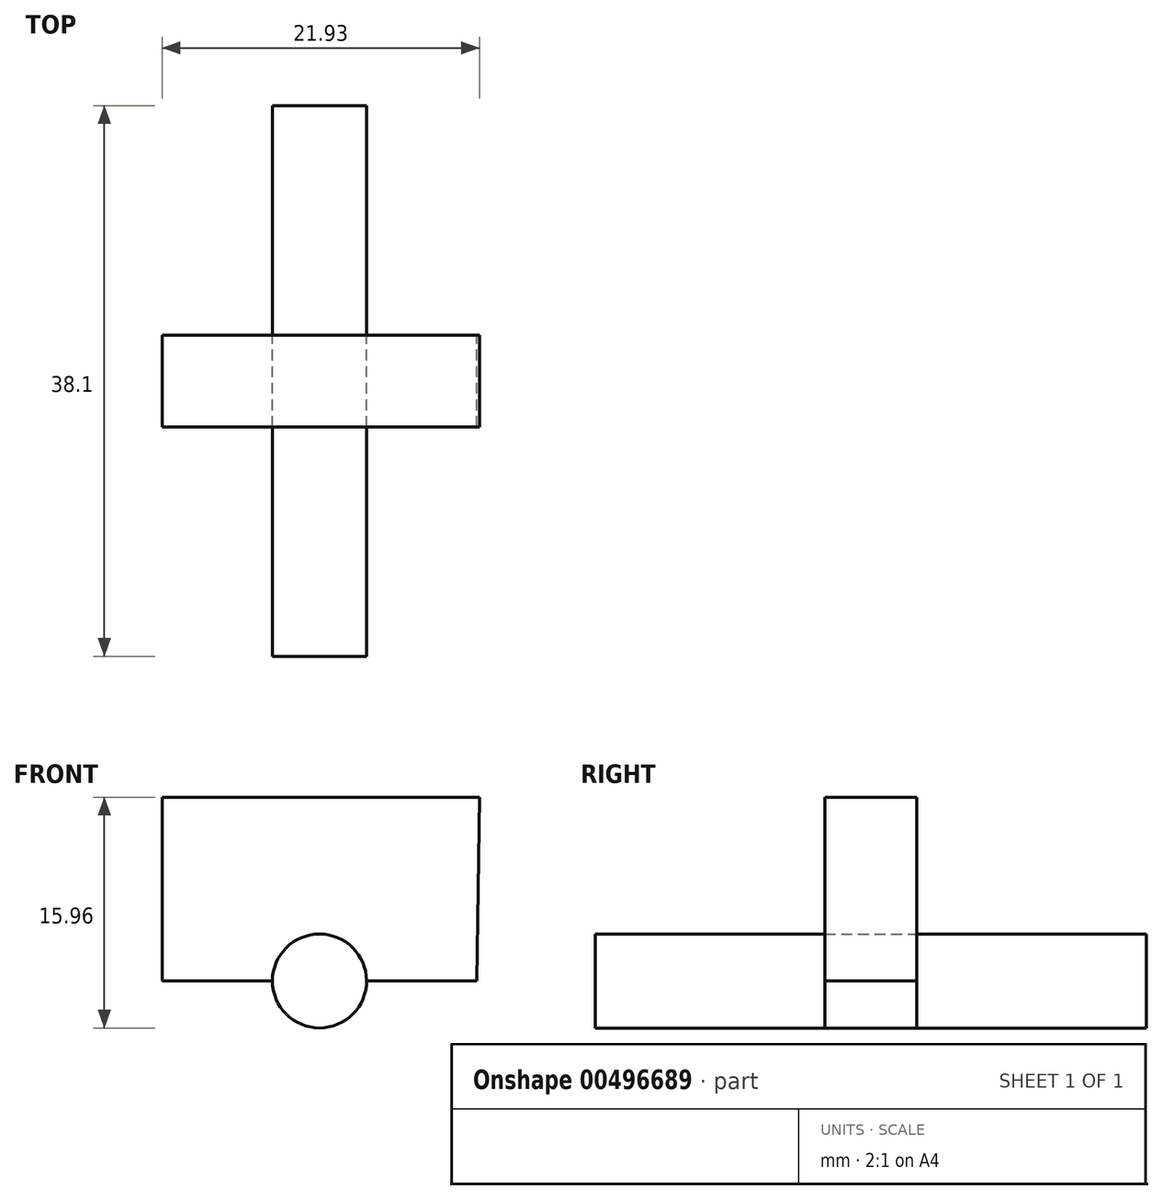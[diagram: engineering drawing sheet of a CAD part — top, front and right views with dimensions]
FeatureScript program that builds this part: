
annotation { "Feature Type Name" : "Feature", "Feature Type Description" : "" }
export const myFeature = defineFeature(function(context is Context, id is Id, definition is map)
    precondition{}
    {
        {
            var Q0;
            Q0=qCreatedBy(makeId("Front.planeOp"),FACE);
            var sketch = newSketch(context, id + "F0", { "sketchPlane" : qUnion([Q0])});
            skCircle(sketch, "E0", {"center": v(-46.67, 40.33) * mm, "radius": 3.26 * mm});
            skArc(sketch, "E1", {"start": v(-43.42, 40.33) * mm, "mid": v(-46.67, 43.57) * mm, "end": v(-49.93, 40.33) * mm});
            skLineSegment(sketch, "E2", {"start": v(-49.93, 40.33) * mm, "end": v(-57.55, 40.33) * mm});
            skLineSegment(sketch, "E3", {"start": v(-57.55, 40.33) * mm, "end": v(-57.55, 53.03) * mm});
            skLineSegment(sketch, "E4", {"start": v(-57.55, 53.03) * mm, "end": v(-35.62, 53.03) * mm});
            skLineSegment(sketch, "E5", {"start": v(-43.42, 40.33) * mm, "end": v(-35.8, 40.33) * mm});
            skLineSegment(sketch, "E6", {"start": v(-35.8, 40.33) * mm, "end": v(-35.62, 53.03) * mm});
            skSolve(sketch);
        }
        {
            var Q0;
            {var subQ0=sQuery(id+"F0.wireOp",EDGE,"E1");Q0=makeQuery(id+"F0.imprint","IMPRINT",FACE,{"disambiguationData":[TD([[makeQuery(id+"F0.imprint","IMPRINT",EDGE,{"derivedFrom":subQ0}),1.0]])]});}
            extrude(context, id + "F1", {"entities" : qUnion([Q0]), "endBound" : BoundingType.SYMMETRIC, "depth" : 38.1 * mm});
        }
        {
            var Q0;
            Q0 = qSketchRegion(id + "F0", true);
            extrude(context, id + "F2", {"entities" : qUnion([Q0]), "endBound" : BoundingType.SYMMETRIC, "depth" : 6.35 * mm});
        }
    });
